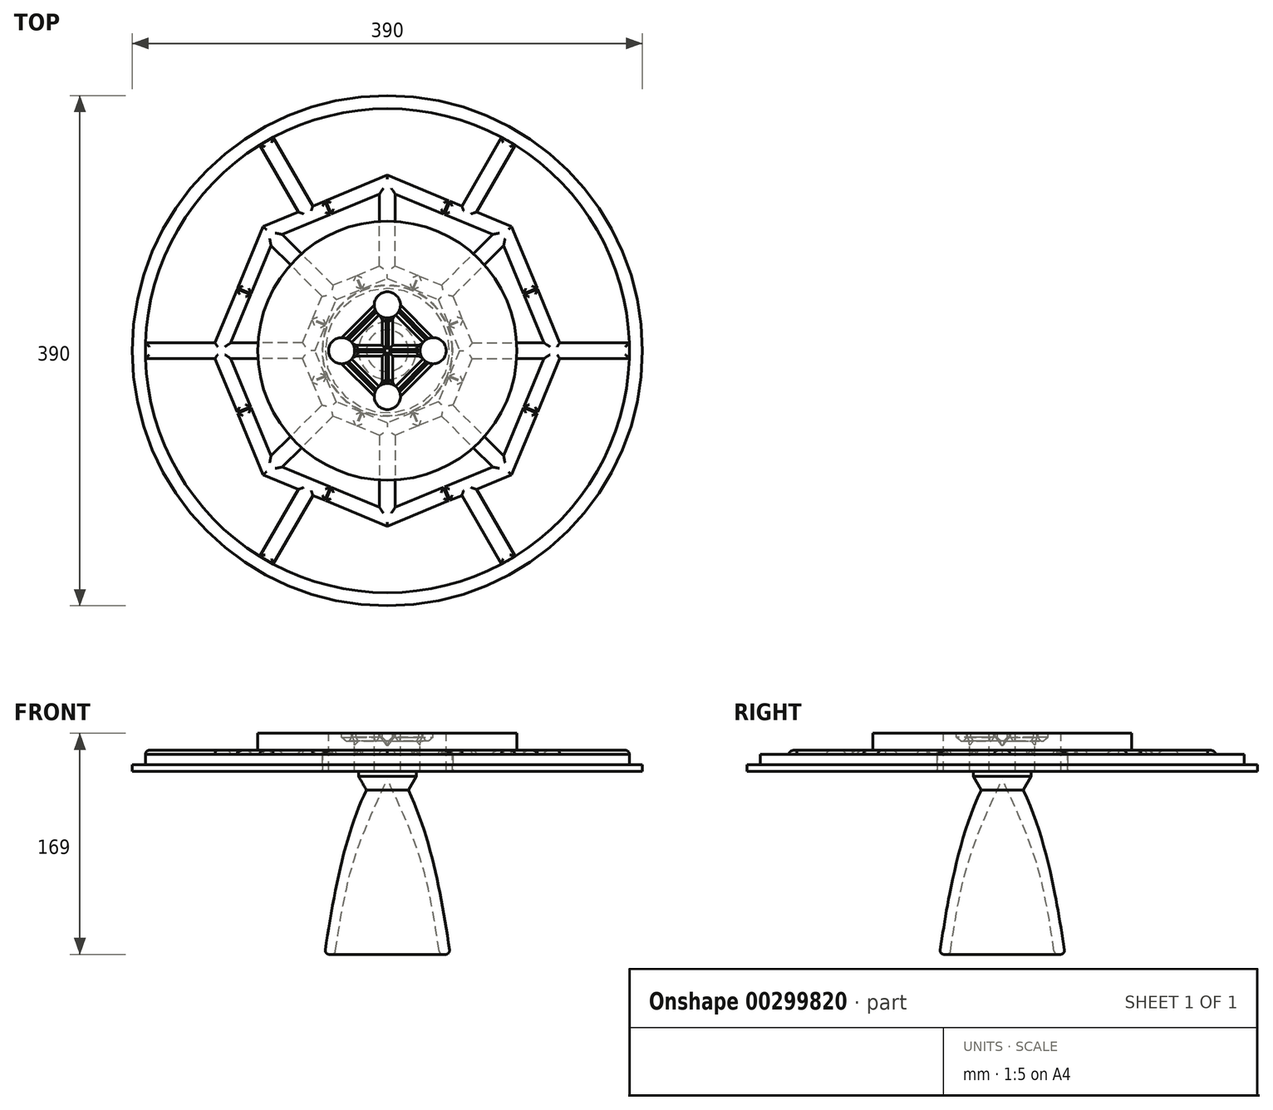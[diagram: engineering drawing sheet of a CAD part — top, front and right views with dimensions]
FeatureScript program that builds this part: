
annotation { "Feature Type Name" : "Feature", "Feature Type Description" : "" }
export const myFeature = defineFeature(function(context is Context, id is Id, definition is map)
    precondition{}
    {
        {
            var Q0;
            Q0=qCreatedBy(makeId("Front.planeOp"),FACE);
            var sketch = newSketch(context, id + "F0", { "sketchPlane" : qUnion([Q0])});
            skLineSegment(sketch, "E0.MirrorCS", {"start": v(50, 0) * mm, "end": v(195, 0) * mm});
            skLineSegment(sketch, "E1", {"start": v(0, 0) * mm, "end": v(0, 0) * mm});
            skLineSegment(sketch, "E2.MirrorCS", {"start": v(195, 0) * mm, "end": v(195, 5) * mm});
            skLineSegment(sketch, "E3.MirrorCS", {"start": v(50, 13) * mm, "end": v(185, 13) * mm});
            skLineSegment(sketch, "E4.MirrorCS", {"start": v(185, 5) * mm, "end": v(195, 5) * mm});
            skLineSegment(sketch, "E5.MirrorCS", {"start": v(185, 13) * mm, "end": v(185, 5) * mm});
            skLineSegment(sketch, "E6.MirrorCS", {"start": v(50, 0) * mm, "end": v(50, 13) * mm});
            skLineSegment(sketch, "E7", {"start": v(0, 0) * mm, "end": v(0, 16.1) * mm});
            skLineSegment(sketch, "E8", {"start": v(0, 0) * mm, "end": v(50, 0) * mm});
            skSolve(sketch);
        }
        {
            var Q0;
            Q0 = qSketchRegion(id + "F0", true);
            var Q1;
            Q1=sQuery(id+"F0.wireOp",EDGE,"E7");
            revolve(context, id + "F1", {"entities" : qUnion([Q0]), "axis" : qUnion([Q1]), "revolveType" : RevolveType.FULL});
        }
        {
            var Q0;
            Q0=makeQuery(id+"F1.opRevolve","SWEPT_FACE",FACE,{"disambiguationData":[OSD([sQuery(id+"F0.wireOp",EDGE,"E3.MirrorCS")])]});
            var sketch = newSketch(context, id + "F2", { "sketchPlane" : qUnion([Q0])});
            skLineSegment(sketch, "E9.0", {"start": v(55.24, 0) * mm, "end": v(47.31, -19.13) * mm});
            skLineSegment(sketch, "E9.7", {"start": v(47.31, 19.13) * mm, "end": v(55.24, 0) * mm});
            skLineSegment(sketch, "E10.0", {"start": v(64.76, -6) * mm, "end": v(57.56, -23.38) * mm});
            skLineSegment(sketch, "E10.7", {"start": v(57.56, 23.38) * mm, "end": v(64.76, 6) * mm});
            skLineSegment(sketch, "E11.0", {"start": v(119.76, -6) * mm, "end": v(104.5, -42.82) * mm});
            skLineSegment(sketch, "E11.7", {"start": v(104.5, 42.82) * mm, "end": v(119.76, 6) * mm});
            skLineSegment(sketch, "E12.0", {"start": v(134.24, 0) * mm, "end": v(114.75, -47.06) * mm});
            skLineSegment(sketch, "E12.7", {"start": v(114.75, 47.06) * mm, "end": v(134.24, 0) * mm});
            skLineSegment(sketch, "E13", {"start": v(64.76, 6) * mm, "end": v(119.76, 6) * mm});
            skLineSegment(sketch, "E14", {"start": v(64.76, -6) * mm, "end": v(119.76, -6) * mm});
            skLineSegment(sketch, "E15", {"start": v(47.31, 19.13) * mm, "end": v(57.56, 23.38) * mm});
            skLineSegment(sketch, "E16", {"start": v(47.31, -19.13) * mm, "end": v(57.56, -23.38) * mm});
            skLineSegment(sketch, "E17.trimOffspring", {"start": v(104.5, 42.82) * mm, "end": v(114.75, 47.06) * mm});
            skLineSegment(sketch, "E18.trimOffspring", {"start": v(104.5, -42.82) * mm, "end": v(114.75, -47.06) * mm});
            skLineSegment(sketch, "E19.1.0", {"start": v(94.92, 94.92) * mm, "end": v(114.42, 47.86) * mm});
            skLineSegment(sketch, "E19.1.1", {"start": v(43.61, 104.17) * mm, "end": v(80.44, 88.92) * mm});
            skLineSegment(sketch, "E19.1.2", {"start": v(46.99, 19.93) * mm, "end": v(57.23, 24.17) * mm});
            skLineSegment(sketch, "E19.1.3", {"start": v(41.55, 50.03) * mm, "end": v(80.44, 88.92) * mm});
            skLineSegment(sketch, "E19.1.4", {"start": v(50.03, 41.55) * mm, "end": v(88.92, 80.44) * mm});
            skLineSegment(sketch, "E19.1.5", {"start": v(50.03, 41.55) * mm, "end": v(57.23, 24.17) * mm});
            skLineSegment(sketch, "E19.1.6", {"start": v(43.61, 104.17) * mm, "end": v(47.86, 114.42) * mm});
            skLineSegment(sketch, "E19.1.7", {"start": v(39.06, 39.06) * mm, "end": v(46.99, 19.93) * mm});
            skLineSegment(sketch, "E19.1.8", {"start": v(47.86, 114.42) * mm, "end": v(94.92, 94.92) * mm});
            skLineSegment(sketch, "E19.1.9", {"start": v(19.93, 46.99) * mm, "end": v(39.06, 39.06) * mm});
            skLineSegment(sketch, "E19.1.10", {"start": v(104.17, 43.61) * mm, "end": v(114.42, 47.86) * mm});
            skLineSegment(sketch, "E19.1.11", {"start": v(24.17, 57.23) * mm, "end": v(41.55, 50.03) * mm});
            skLineSegment(sketch, "E19.1.12", {"start": v(88.92, 80.44) * mm, "end": v(104.17, 43.61) * mm});
            skLineSegment(sketch, "E19.1.13", {"start": v(19.93, 46.99) * mm, "end": v(24.17, 57.23) * mm});
            skLineSegment(sketch, "E19.2.0", {"start": v(0, 134.24) * mm, "end": v(47.06, 114.75) * mm});
            skLineSegment(sketch, "E19.2.1", {"start": v(-42.82, 104.5) * mm, "end": v(-6, 119.76) * mm});
            skLineSegment(sketch, "E19.2.2", {"start": v(19.13, 47.31) * mm, "end": v(23.38, 57.56) * mm});
            skLineSegment(sketch, "E19.2.3", {"start": v(-6, 64.76) * mm, "end": v(-6, 119.76) * mm});
            skLineSegment(sketch, "E19.2.4", {"start": v(6, 64.76) * mm, "end": v(6, 119.76) * mm});
            skLineSegment(sketch, "E19.2.5", {"start": v(6, 64.76) * mm, "end": v(23.38, 57.56) * mm});
            skLineSegment(sketch, "E19.2.6", {"start": v(-42.82, 104.5) * mm, "end": v(-47.06, 114.75) * mm});
            skLineSegment(sketch, "E19.2.7", {"start": v(0, 55.24) * mm, "end": v(19.13, 47.31) * mm});
            skLineSegment(sketch, "E19.2.8", {"start": v(-47.06, 114.75) * mm, "end": v(0, 134.24) * mm});
            skLineSegment(sketch, "E19.2.9", {"start": v(-19.13, 47.31) * mm, "end": v(0, 55.24) * mm});
            skLineSegment(sketch, "E19.2.10", {"start": v(42.82, 104.5) * mm, "end": v(47.06, 114.75) * mm});
            skLineSegment(sketch, "E19.2.11", {"start": v(-23.38, 57.56) * mm, "end": v(-6, 64.76) * mm});
            skLineSegment(sketch, "E19.2.12", {"start": v(6, 119.76) * mm, "end": v(42.82, 104.5) * mm});
            skLineSegment(sketch, "E19.2.13", {"start": v(-19.13, 47.31) * mm, "end": v(-23.38, 57.56) * mm});
            skLineSegment(sketch, "E19.3.0", {"start": v(-94.92, 94.92) * mm, "end": v(-47.86, 114.42) * mm});
            skLineSegment(sketch, "E19.3.1", {"start": v(-104.17, 43.61) * mm, "end": v(-88.92, 80.44) * mm});
            skLineSegment(sketch, "E19.3.2", {"start": v(-19.93, 46.99) * mm, "end": v(-24.17, 57.23) * mm});
            skLineSegment(sketch, "E19.3.3", {"start": v(-50.03, 41.55) * mm, "end": v(-88.92, 80.44) * mm});
            skLineSegment(sketch, "E19.3.4", {"start": v(-41.55, 50.03) * mm, "end": v(-80.44, 88.92) * mm});
            skLineSegment(sketch, "E19.3.5", {"start": v(-41.55, 50.03) * mm, "end": v(-24.17, 57.23) * mm});
            skLineSegment(sketch, "E19.3.6", {"start": v(-104.17, 43.61) * mm, "end": v(-114.42, 47.86) * mm});
            skLineSegment(sketch, "E19.3.7", {"start": v(-39.06, 39.06) * mm, "end": v(-19.93, 46.99) * mm});
            skLineSegment(sketch, "E19.3.8", {"start": v(-114.42, 47.86) * mm, "end": v(-94.92, 94.92) * mm});
            skLineSegment(sketch, "E19.3.9", {"start": v(-46.99, 19.93) * mm, "end": v(-39.06, 39.06) * mm});
            skLineSegment(sketch, "E19.3.10", {"start": v(-43.61, 104.17) * mm, "end": v(-47.86, 114.42) * mm});
            skLineSegment(sketch, "E19.3.11", {"start": v(-57.23, 24.17) * mm, "end": v(-50.03, 41.55) * mm});
            skLineSegment(sketch, "E19.3.12", {"start": v(-80.44, 88.92) * mm, "end": v(-43.61, 104.17) * mm});
            skLineSegment(sketch, "E19.3.13", {"start": v(-46.99, 19.93) * mm, "end": v(-57.23, 24.17) * mm});
            skLineSegment(sketch, "E19.4.0", {"start": v(-134.24, 0) * mm, "end": v(-114.75, 47.06) * mm});
            skLineSegment(sketch, "E19.4.1", {"start": v(-104.5, -42.82) * mm, "end": v(-119.76, -6) * mm});
            skLineSegment(sketch, "E19.4.2", {"start": v(-47.31, 19.13) * mm, "end": v(-57.56, 23.38) * mm});
            skLineSegment(sketch, "E19.4.3", {"start": v(-64.76, -6) * mm, "end": v(-119.76, -6) * mm});
            skLineSegment(sketch, "E19.4.4", {"start": v(-64.76, 6) * mm, "end": v(-119.76, 6) * mm});
            skLineSegment(sketch, "E19.4.5", {"start": v(-64.76, 6) * mm, "end": v(-57.56, 23.38) * mm});
            skLineSegment(sketch, "E19.4.6", {"start": v(-104.5, -42.82) * mm, "end": v(-114.75, -47.06) * mm});
            skLineSegment(sketch, "E19.4.7", {"start": v(-55.24, 0) * mm, "end": v(-47.31, 19.13) * mm});
            skLineSegment(sketch, "E19.4.8", {"start": v(-114.75, -47.06) * mm, "end": v(-134.24, 0) * mm});
            skLineSegment(sketch, "E19.4.9", {"start": v(-47.31, -19.13) * mm, "end": v(-55.24, 0) * mm});
            skLineSegment(sketch, "E19.4.10", {"start": v(-104.5, 42.82) * mm, "end": v(-114.75, 47.06) * mm});
            skLineSegment(sketch, "E19.4.11", {"start": v(-57.56, -23.38) * mm, "end": v(-64.76, -6) * mm});
            skLineSegment(sketch, "E19.4.12", {"start": v(-119.76, 6) * mm, "end": v(-104.5, 42.82) * mm});
            skLineSegment(sketch, "E19.4.13", {"start": v(-47.31, -19.13) * mm, "end": v(-57.56, -23.38) * mm});
            skLineSegment(sketch, "E19.5.0", {"start": v(-94.92, -94.92) * mm, "end": v(-114.42, -47.86) * mm});
            skLineSegment(sketch, "E19.5.1", {"start": v(-43.61, -104.17) * mm, "end": v(-80.44, -88.92) * mm});
            skLineSegment(sketch, "E19.5.2", {"start": v(-46.99, -19.93) * mm, "end": v(-57.23, -24.17) * mm});
            skLineSegment(sketch, "E19.5.3", {"start": v(-41.55, -50.03) * mm, "end": v(-80.44, -88.92) * mm});
            skLineSegment(sketch, "E19.5.4", {"start": v(-50.03, -41.55) * mm, "end": v(-88.92, -80.44) * mm});
            skLineSegment(sketch, "E19.5.5", {"start": v(-50.03, -41.55) * mm, "end": v(-57.23, -24.17) * mm});
            skLineSegment(sketch, "E19.5.6", {"start": v(-43.61, -104.17) * mm, "end": v(-47.86, -114.42) * mm});
            skLineSegment(sketch, "E19.5.7", {"start": v(-39.06, -39.06) * mm, "end": v(-46.99, -19.93) * mm});
            skLineSegment(sketch, "E19.5.8", {"start": v(-47.86, -114.42) * mm, "end": v(-94.92, -94.92) * mm});
            skLineSegment(sketch, "E19.5.9", {"start": v(-19.93, -46.99) * mm, "end": v(-39.06, -39.06) * mm});
            skLineSegment(sketch, "E19.5.10", {"start": v(-104.17, -43.61) * mm, "end": v(-114.42, -47.86) * mm});
            skLineSegment(sketch, "E19.5.11", {"start": v(-24.17, -57.23) * mm, "end": v(-41.55, -50.03) * mm});
            skLineSegment(sketch, "E19.5.12", {"start": v(-88.92, -80.44) * mm, "end": v(-104.17, -43.61) * mm});
            skLineSegment(sketch, "E19.5.13", {"start": v(-19.93, -46.99) * mm, "end": v(-24.17, -57.23) * mm});
            skLineSegment(sketch, "E19.6.0", {"start": v(0, -134.24) * mm, "end": v(-47.06, -114.75) * mm});
            skLineSegment(sketch, "E19.6.1", {"start": v(42.82, -104.5) * mm, "end": v(6, -119.76) * mm});
            skLineSegment(sketch, "E19.6.2", {"start": v(-19.13, -47.31) * mm, "end": v(-23.38, -57.56) * mm});
            skLineSegment(sketch, "E19.6.3", {"start": v(6, -64.76) * mm, "end": v(6, -119.76) * mm});
            skLineSegment(sketch, "E19.6.4", {"start": v(-6, -64.76) * mm, "end": v(-6, -119.76) * mm});
            skLineSegment(sketch, "E19.6.5", {"start": v(-6, -64.76) * mm, "end": v(-23.38, -57.56) * mm});
            skLineSegment(sketch, "E19.6.6", {"start": v(42.82, -104.5) * mm, "end": v(47.06, -114.75) * mm});
            skLineSegment(sketch, "E19.6.7", {"start": v(0, -55.24) * mm, "end": v(-19.13, -47.31) * mm});
            skLineSegment(sketch, "E19.6.8", {"start": v(47.06, -114.75) * mm, "end": v(0, -134.24) * mm});
            skLineSegment(sketch, "E19.6.9", {"start": v(19.13, -47.31) * mm, "end": v(0, -55.24) * mm});
            skLineSegment(sketch, "E19.6.10", {"start": v(-42.82, -104.5) * mm, "end": v(-47.06, -114.75) * mm});
            skLineSegment(sketch, "E19.6.11", {"start": v(23.38, -57.56) * mm, "end": v(6, -64.76) * mm});
            skLineSegment(sketch, "E19.6.12", {"start": v(-6, -119.76) * mm, "end": v(-42.82, -104.5) * mm});
            skLineSegment(sketch, "E19.6.13", {"start": v(19.13, -47.31) * mm, "end": v(23.38, -57.56) * mm});
            skLineSegment(sketch, "E19.7.0", {"start": v(94.92, -94.92) * mm, "end": v(47.86, -114.42) * mm});
            skLineSegment(sketch, "E19.7.1", {"start": v(104.17, -43.61) * mm, "end": v(88.92, -80.44) * mm});
            skLineSegment(sketch, "E19.7.2", {"start": v(19.93, -46.99) * mm, "end": v(24.17, -57.23) * mm});
            skLineSegment(sketch, "E19.7.3", {"start": v(50.03, -41.55) * mm, "end": v(88.92, -80.44) * mm});
            skLineSegment(sketch, "E19.7.4", {"start": v(41.55, -50.03) * mm, "end": v(80.44, -88.92) * mm});
            skLineSegment(sketch, "E19.7.5", {"start": v(41.55, -50.03) * mm, "end": v(24.17, -57.23) * mm});
            skLineSegment(sketch, "E19.7.6", {"start": v(104.17, -43.61) * mm, "end": v(114.42, -47.86) * mm});
            skLineSegment(sketch, "E19.7.7", {"start": v(39.06, -39.06) * mm, "end": v(19.93, -46.99) * mm});
            skLineSegment(sketch, "E19.7.8", {"start": v(114.42, -47.86) * mm, "end": v(94.92, -94.92) * mm});
            skLineSegment(sketch, "E19.7.9", {"start": v(46.99, -19.93) * mm, "end": v(39.06, -39.06) * mm});
            skLineSegment(sketch, "E19.7.10", {"start": v(43.61, -104.17) * mm, "end": v(47.86, -114.42) * mm});
            skLineSegment(sketch, "E19.7.11", {"start": v(57.23, -24.17) * mm, "end": v(50.03, -41.55) * mm});
            skLineSegment(sketch, "E19.7.12", {"start": v(80.44, -88.92) * mm, "end": v(43.61, -104.17) * mm});
            skLineSegment(sketch, "E19.7.13", {"start": v(46.99, -19.93) * mm, "end": v(57.23, -24.17) * mm});
            skPoint(sketch, "E19.center", {"position": v(0, 0) * mm});
            skSolve(sketch);
        }
        {
            var Q0;
            Q0 = qSketchRegion(id + "F2", true);
            extrude(context, id + "F3", {"entities" : qUnion([Q0]), "operationType" : NewBodyOperationType.ADD, "depth" : 3 * mm});
        }
        {
            var Q0;
            Q0=makeQuery(id+"F1.opRevolve","SWEPT_FACE",FACE,{"disambiguationData":[OSD([sQuery(id+"F0.wireOp",EDGE,"E3.MirrorCS")])]});
            var sketch = newSketch(context, id + "F4", { "sketchPlane" : qUnion([Q0])});
            skLineSegment(sketch, "E20", {"start": v(119.9, 0) * mm, "end": v(119.9, -6) * mm});
            skLineSegment(sketch, "E21", {"start": v(119.9, -6) * mm, "end": v(184.9, -6) * mm});
            skLineSegment(sketch, "E22.MirrorCS", {"start": v(119.9, 6) * mm, "end": v(184.9, 6) * mm});
            skLineSegment(sketch, "E23.MirrorCS", {"start": v(119.9, 0) * mm, "end": v(119.9, 6) * mm});
            skLineSegment(sketch, "E24", {"start": v(184.9, 6) * mm, "end": v(184.9, -6) * mm});
            skLineSegment(sketch, "E25.1.0", {"start": v(87.26, 163.13) * mm, "end": v(97.65, 157.13) * mm});
            skLineSegment(sketch, "E25.1.1", {"start": v(65.15, 100.84) * mm, "end": v(97.65, 157.13) * mm});
            skLineSegment(sketch, "E25.1.2", {"start": v(59.95, 103.84) * mm, "end": v(54.76, 106.84) * mm});
            skLineSegment(sketch, "E25.1.3", {"start": v(59.95, 103.84) * mm, "end": v(65.15, 100.84) * mm});
            skLineSegment(sketch, "E25.1.4", {"start": v(54.76, 106.84) * mm, "end": v(87.26, 163.13) * mm});
            skLineSegment(sketch, "E25.2.0", {"start": v(-97.65, 157.13) * mm, "end": v(-87.26, 163.13) * mm});
            skLineSegment(sketch, "E25.2.1", {"start": v(-54.76, 106.84) * mm, "end": v(-87.26, 163.13) * mm});
            skLineSegment(sketch, "E25.2.2", {"start": v(-59.95, 103.84) * mm, "end": v(-65.15, 100.84) * mm});
            skLineSegment(sketch, "E25.2.3", {"start": v(-59.95, 103.84) * mm, "end": v(-54.76, 106.84) * mm});
            skLineSegment(sketch, "E25.2.4", {"start": v(-65.15, 100.84) * mm, "end": v(-97.65, 157.13) * mm});
            skLineSegment(sketch, "E25.3.0", {"start": v(-184.9, -6) * mm, "end": v(-184.9, 6) * mm});
            skLineSegment(sketch, "E25.3.1", {"start": v(-119.9, 6) * mm, "end": v(-184.9, 6) * mm});
            skLineSegment(sketch, "E25.3.2", {"start": v(-119.9, 0) * mm, "end": v(-119.9, -6) * mm});
            skLineSegment(sketch, "E25.3.3", {"start": v(-119.9, 0) * mm, "end": v(-119.9, 6) * mm});
            skLineSegment(sketch, "E25.3.4", {"start": v(-119.9, -6) * mm, "end": v(-184.9, -6) * mm});
            skLineSegment(sketch, "E25.4.0", {"start": v(-87.26, -163.13) * mm, "end": v(-97.65, -157.13) * mm});
            skLineSegment(sketch, "E25.4.1", {"start": v(-65.15, -100.84) * mm, "end": v(-97.65, -157.13) * mm});
            skLineSegment(sketch, "E25.4.2", {"start": v(-59.95, -103.84) * mm, "end": v(-54.76, -106.84) * mm});
            skLineSegment(sketch, "E25.4.3", {"start": v(-59.95, -103.84) * mm, "end": v(-65.15, -100.84) * mm});
            skLineSegment(sketch, "E25.4.4", {"start": v(-54.76, -106.84) * mm, "end": v(-87.26, -163.13) * mm});
            skLineSegment(sketch, "E25.5.0", {"start": v(97.65, -157.13) * mm, "end": v(87.26, -163.13) * mm});
            skLineSegment(sketch, "E25.5.1", {"start": v(54.76, -106.84) * mm, "end": v(87.26, -163.13) * mm});
            skLineSegment(sketch, "E25.5.2", {"start": v(59.95, -103.84) * mm, "end": v(65.15, -100.84) * mm});
            skLineSegment(sketch, "E25.5.3", {"start": v(59.95, -103.84) * mm, "end": v(54.76, -106.84) * mm});
            skLineSegment(sketch, "E25.5.4", {"start": v(65.15, -100.84) * mm, "end": v(97.65, -157.13) * mm});
            skPoint(sketch, "E25.center", {"position": v(0, 0) * mm});
            skSolve(sketch);
        }
        {
            var Q0;
            Q0 = qSketchRegion(id + "F4", true);
            extrude(context, id + "F5", {"entities" : qUnion([Q0]), "operationType" : NewBodyOperationType.ADD, "depth" : 3 * mm});
        }
        {
            var Q0;
            Q0=makeQuery(id+"F5.boolean.opBoolean","MERGE",FACE,{"derivedFrom":[makeQuery(id+"F3.opExtrude","CAP_FACE",FACE,{"disambiguationData":[OSD([sQuery(id+"F2.wireOp",EDGE,"E19.4.0"),sQuery(id+"F2.wireOp",EDGE,"E19.4.1"),sQuery(id+"F2.wireOp",EDGE,"E19.4.2"),sQuery(id+"F2.wireOp",EDGE,"E19.4.3"),sQuery(id+"F2.wireOp",EDGE,"E19.4.4"),sQuery(id+"F2.wireOp",EDGE,"E19.4.5"),sQuery(id+"F2.wireOp",EDGE,"E19.4.6"),sQuery(id+"F2.wireOp",EDGE,"E19.4.7"),sQuery(id+"F2.wireOp",EDGE,"E19.4.8"),sQuery(id+"F2.wireOp",EDGE,"E19.4.9"),sQuery(id+"F2.wireOp",EDGE,"E19.4.10"),sQuery(id+"F2.wireOp",EDGE,"E19.4.11"),sQuery(id+"F2.wireOp",EDGE,"E19.4.12"),sQuery(id+"F2.wireOp",EDGE,"E19.4.13")])],"isStart":false}),makeQuery(id+"F5.opExtrude","CAP_FACE",FACE,{"disambiguationData":[OSD([sQuery(id+"F4.wireOp",EDGE,"E25.3.0"),sQuery(id+"F4.wireOp",EDGE,"E25.3.1"),sQuery(id+"F4.wireOp",EDGE,"E25.3.2"),sQuery(id+"F4.wireOp",EDGE,"E25.3.3"),sQuery(id+"F4.wireOp",EDGE,"E25.3.4")])],"isStart":false})]});
            var Q1;
            Q1=makeQuery(id+"F5.boolean.opBoolean","MERGE",FACE,{"derivedFrom":[makeQuery(id+"F3.opExtrude","CAP_FACE",FACE,{"disambiguationData":[OSD([sQuery(id+"F2.wireOp",EDGE,"E19.3.0"),sQuery(id+"F2.wireOp",EDGE,"E19.3.1"),sQuery(id+"F2.wireOp",EDGE,"E19.3.2"),sQuery(id+"F2.wireOp",EDGE,"E19.3.3"),sQuery(id+"F2.wireOp",EDGE,"E19.3.4"),sQuery(id+"F2.wireOp",EDGE,"E19.3.5"),sQuery(id+"F2.wireOp",EDGE,"E19.3.6"),sQuery(id+"F2.wireOp",EDGE,"E19.3.7"),sQuery(id+"F2.wireOp",EDGE,"E19.3.8"),sQuery(id+"F2.wireOp",EDGE,"E19.3.9"),sQuery(id+"F2.wireOp",EDGE,"E19.3.10"),sQuery(id+"F2.wireOp",EDGE,"E19.3.11"),sQuery(id+"F2.wireOp",EDGE,"E19.3.12"),sQuery(id+"F2.wireOp",EDGE,"E19.3.13")])],"isStart":false}),makeQuery(id+"F5.opExtrude","CAP_FACE",FACE,{"disambiguationData":[OSD([sQuery(id+"F4.wireOp",EDGE,"E25.2.0"),sQuery(id+"F4.wireOp",EDGE,"E25.2.1"),sQuery(id+"F4.wireOp",EDGE,"E25.2.2"),sQuery(id+"F4.wireOp",EDGE,"E25.2.3"),sQuery(id+"F4.wireOp",EDGE,"E25.2.4")])],"isStart":false})]});
            var Q2;
            Q2=makeQuery(id+"F3.opExtrude","CAP_FACE",FACE,{"disambiguationData":[OSD([sQuery(id+"F2.wireOp",EDGE,"E19.2.0"),sQuery(id+"F2.wireOp",EDGE,"E19.2.1"),sQuery(id+"F2.wireOp",EDGE,"E19.2.2"),sQuery(id+"F2.wireOp",EDGE,"E19.2.3"),sQuery(id+"F2.wireOp",EDGE,"E19.2.4"),sQuery(id+"F2.wireOp",EDGE,"E19.2.5"),sQuery(id+"F2.wireOp",EDGE,"E19.2.6"),sQuery(id+"F2.wireOp",EDGE,"E19.2.7"),sQuery(id+"F2.wireOp",EDGE,"E19.2.8"),sQuery(id+"F2.wireOp",EDGE,"E19.2.9"),sQuery(id+"F2.wireOp",EDGE,"E19.2.10"),sQuery(id+"F2.wireOp",EDGE,"E19.2.11"),sQuery(id+"F2.wireOp",EDGE,"E19.2.12"),sQuery(id+"F2.wireOp",EDGE,"E19.2.13")])],"isStart":false});
            var Q3;
            Q3=makeQuery(id+"F5.boolean.opBoolean","MERGE",FACE,{"derivedFrom":[makeQuery(id+"F3.opExtrude","CAP_FACE",FACE,{"disambiguationData":[OSD([sQuery(id+"F2.wireOp",EDGE,"E19.1.0"),sQuery(id+"F2.wireOp",EDGE,"E19.1.1"),sQuery(id+"F2.wireOp",EDGE,"E19.1.2"),sQuery(id+"F2.wireOp",EDGE,"E19.1.3"),sQuery(id+"F2.wireOp",EDGE,"E19.1.4"),sQuery(id+"F2.wireOp",EDGE,"E19.1.5"),sQuery(id+"F2.wireOp",EDGE,"E19.1.6"),sQuery(id+"F2.wireOp",EDGE,"E19.1.7"),sQuery(id+"F2.wireOp",EDGE,"E19.1.8"),sQuery(id+"F2.wireOp",EDGE,"E19.1.9"),sQuery(id+"F2.wireOp",EDGE,"E19.1.10"),sQuery(id+"F2.wireOp",EDGE,"E19.1.11"),sQuery(id+"F2.wireOp",EDGE,"E19.1.12"),sQuery(id+"F2.wireOp",EDGE,"E19.1.13")])],"isStart":false}),makeQuery(id+"F5.opExtrude","CAP_FACE",FACE,{"disambiguationData":[OSD([sQuery(id+"F4.wireOp",EDGE,"E25.1.0"),sQuery(id+"F4.wireOp",EDGE,"E25.1.1"),sQuery(id+"F4.wireOp",EDGE,"E25.1.2"),sQuery(id+"F4.wireOp",EDGE,"E25.1.3"),sQuery(id+"F4.wireOp",EDGE,"E25.1.4")])],"isStart":false})]});
            var Q4;
            Q4=makeQuery(id+"F5.boolean.opBoolean","MERGE",FACE,{"derivedFrom":[makeQuery(id+"F3.opExtrude","CAP_FACE",FACE,{"disambiguationData":[OSD([sQuery(id+"F2.wireOp",EDGE,"E9.0"),sQuery(id+"F2.wireOp",EDGE,"E9.7"),sQuery(id+"F2.wireOp",EDGE,"E10.0"),sQuery(id+"F2.wireOp",EDGE,"E10.7"),sQuery(id+"F2.wireOp",EDGE,"E11.0"),sQuery(id+"F2.wireOp",EDGE,"E11.7"),sQuery(id+"F2.wireOp",EDGE,"E12.0"),sQuery(id+"F2.wireOp",EDGE,"E12.7"),sQuery(id+"F2.wireOp",EDGE,"E13"),sQuery(id+"F2.wireOp",EDGE,"E14"),sQuery(id+"F2.wireOp",EDGE,"E15"),sQuery(id+"F2.wireOp",EDGE,"E16"),sQuery(id+"F2.wireOp",EDGE,"E17.trimOffspring"),sQuery(id+"F2.wireOp",EDGE,"E18.trimOffspring")])],"isStart":false}),makeQuery(id+"F5.opExtrude","CAP_FACE",FACE,{"disambiguationData":[OSD([sQuery(id+"F4.wireOp",EDGE,"E20"),sQuery(id+"F4.wireOp",EDGE,"E21"),sQuery(id+"F4.wireOp",EDGE,"E22.MirrorCS"),sQuery(id+"F4.wireOp",EDGE,"E23.MirrorCS"),sQuery(id+"F4.wireOp",EDGE,"E24")])],"isStart":false})]});
            var Q5;
            Q5=makeQuery(id+"F5.boolean.opBoolean","MERGE",FACE,{"derivedFrom":[makeQuery(id+"F3.opExtrude","CAP_FACE",FACE,{"disambiguationData":[OSD([sQuery(id+"F2.wireOp",EDGE,"E19.7.0"),sQuery(id+"F2.wireOp",EDGE,"E19.7.1"),sQuery(id+"F2.wireOp",EDGE,"E19.7.2"),sQuery(id+"F2.wireOp",EDGE,"E19.7.3"),sQuery(id+"F2.wireOp",EDGE,"E19.7.4"),sQuery(id+"F2.wireOp",EDGE,"E19.7.5"),sQuery(id+"F2.wireOp",EDGE,"E19.7.6"),sQuery(id+"F2.wireOp",EDGE,"E19.7.7"),sQuery(id+"F2.wireOp",EDGE,"E19.7.8"),sQuery(id+"F2.wireOp",EDGE,"E19.7.9"),sQuery(id+"F2.wireOp",EDGE,"E19.7.10"),sQuery(id+"F2.wireOp",EDGE,"E19.7.11"),sQuery(id+"F2.wireOp",EDGE,"E19.7.12"),sQuery(id+"F2.wireOp",EDGE,"E19.7.13")])],"isStart":false}),makeQuery(id+"F5.opExtrude","CAP_FACE",FACE,{"disambiguationData":[OSD([sQuery(id+"F4.wireOp",EDGE,"E25.5.0"),sQuery(id+"F4.wireOp",EDGE,"E25.5.1"),sQuery(id+"F4.wireOp",EDGE,"E25.5.2"),sQuery(id+"F4.wireOp",EDGE,"E25.5.3"),sQuery(id+"F4.wireOp",EDGE,"E25.5.4")])],"isStart":false})]});
            var Q6;
            Q6=makeQuery(id+"F3.opExtrude","CAP_FACE",FACE,{"disambiguationData":[OSD([sQuery(id+"F2.wireOp",EDGE,"E19.6.0"),sQuery(id+"F2.wireOp",EDGE,"E19.6.1"),sQuery(id+"F2.wireOp",EDGE,"E19.6.2"),sQuery(id+"F2.wireOp",EDGE,"E19.6.3"),sQuery(id+"F2.wireOp",EDGE,"E19.6.4"),sQuery(id+"F2.wireOp",EDGE,"E19.6.5"),sQuery(id+"F2.wireOp",EDGE,"E19.6.6"),sQuery(id+"F2.wireOp",EDGE,"E19.6.7"),sQuery(id+"F2.wireOp",EDGE,"E19.6.8"),sQuery(id+"F2.wireOp",EDGE,"E19.6.9"),sQuery(id+"F2.wireOp",EDGE,"E19.6.10"),sQuery(id+"F2.wireOp",EDGE,"E19.6.11"),sQuery(id+"F2.wireOp",EDGE,"E19.6.12"),sQuery(id+"F2.wireOp",EDGE,"E19.6.13")])],"isStart":false});
            var Q7;
            Q7=makeQuery(id+"F5.boolean.opBoolean","MERGE",FACE,{"derivedFrom":[makeQuery(id+"F3.opExtrude","CAP_FACE",FACE,{"disambiguationData":[OSD([sQuery(id+"F2.wireOp",EDGE,"E19.5.0"),sQuery(id+"F2.wireOp",EDGE,"E19.5.1"),sQuery(id+"F2.wireOp",EDGE,"E19.5.2"),sQuery(id+"F2.wireOp",EDGE,"E19.5.3"),sQuery(id+"F2.wireOp",EDGE,"E19.5.4"),sQuery(id+"F2.wireOp",EDGE,"E19.5.5"),sQuery(id+"F2.wireOp",EDGE,"E19.5.6"),sQuery(id+"F2.wireOp",EDGE,"E19.5.7"),sQuery(id+"F2.wireOp",EDGE,"E19.5.8"),sQuery(id+"F2.wireOp",EDGE,"E19.5.9"),sQuery(id+"F2.wireOp",EDGE,"E19.5.10"),sQuery(id+"F2.wireOp",EDGE,"E19.5.11"),sQuery(id+"F2.wireOp",EDGE,"E19.5.12"),sQuery(id+"F2.wireOp",EDGE,"E19.5.13")])],"isStart":false}),makeQuery(id+"F5.opExtrude","CAP_FACE",FACE,{"disambiguationData":[OSD([sQuery(id+"F4.wireOp",EDGE,"E25.4.0"),sQuery(id+"F4.wireOp",EDGE,"E25.4.1"),sQuery(id+"F4.wireOp",EDGE,"E25.4.2"),sQuery(id+"F4.wireOp",EDGE,"E25.4.3"),sQuery(id+"F4.wireOp",EDGE,"E25.4.4")])],"isStart":false})]});
            fillet(context, id + "F6", {"entities" : qUnion([Q0, Q1, Q2, Q3, Q4, Q5, Q6, Q7]), "radius" : 3 * mm, "tangentPropagation" : true, "allowEdgeOverflow" : false});
        }
        {
            var Q0;
            Q0=qCreatedBy(makeId("Front.planeOp"),FACE);
            var sketch = newSketch(context, id + "F7", { "sketchPlane" : qUnion([Q0])});
            skLineSegment(sketch, "E26", {"start": v(0, 0) * mm, "end": v(0, 29) * mm});
            skLineSegment(sketch, "E27", {"start": v(0, 29) * mm, "end": v(99, 29) * mm});
            skLineSegment(sketch, "E28", {"start": v(99, 29) * mm, "end": v(99, 16) * mm});
            skLineSegment(sketch, "E29", {"start": v(99, 16) * mm, "end": v(49.6, 16) * mm});
            skLineSegment(sketch, "E30", {"start": v(49.6, 16) * mm, "end": v(49.6, 0) * mm});
            skLineSegment(sketch, "E31", {"start": v(22, 0) * mm, "end": v(22, -4) * mm});
            skLineSegment(sketch, "E32", {"start": v(22, -4) * mm, "end": v(16, -14.4) * mm});
            skLineSegment(sketch, "E33", {"start": v(0, 0) * mm, "end": v(0, -6) * mm});
            skFitSpline(sketch, "E34", {"points": [v(16, -14.4) * mm, v(35.04, -70) * mm, v(48, -140) * mm], "startDerivative": vector(47.96, -98.6) * mm, "endDerivative": vector(18.7, -125.17) * mm});
            skFitSpline(sketch, "E35", {"points": [v(40, -140) * mm, v(26.13, -70) * mm, v(0, -6) * mm], "startDerivative": vector(-21.37, 141.56) * mm, "endDerivative": vector(-58.69, 128.47) * mm});
            skLineSegment(sketch, "E36", {"start": v(40, -140) * mm, "end": v(48, -140) * mm});
            skLineSegment(sketch, "E37", {"start": v(22, 0) * mm, "end": v(49.6, 0) * mm});
            skSolve(sketch);
        }
        {
            var Q0;
            Q0 = qSketchRegion(id + "F7", true);
            var Q1;
            Q1=sQuery(id+"F7.wireOp",EDGE,"E26");
            revolve(context, id + "F8", {"entities" : qUnion([Q0]), "axis" : qUnion([Q1]), "revolveType" : RevolveType.FULL});
        }
        {
            var Q0;
            Q0=makeQuery(id+"F8.opRevolve","SWEPT_FACE",FACE,{"disambiguationData":[OSD([sQuery(id+"F7.wireOp",EDGE,"E36")])]});
            fillet(context, id + "F9", {"entities" : qUnion([Q0]), "radius" : 3 * mm, "tangentPropagation" : true, "allowEdgeOverflow" : false});
        }
        {
            var Q0;
            Q0=makeQuery(id+"F8.opRevolve","SWEPT_FACE",FACE,{"disambiguationData":[OSD([sQuery(id+"F7.wireOp",EDGE,"E27")])]});
            var sketch = newSketch(context, id + "F10", { "sketchPlane" : qUnion([Q0])});
            skCircle(sketch, "E38", {"center": v(35, 0) * mm, "radius": 10 * mm});
            skCircle(sketch, "E39.1.0", {"center": v(0, 35) * mm, "radius": 10 * mm});
            skCircle(sketch, "E39.2.0", {"center": v(-35, 0) * mm, "radius": 10 * mm});
            skCircle(sketch, "E39.3.0", {"center": v(0, -35) * mm, "radius": 10 * mm});
            skPoint(sketch, "E39.center", {"position": v(0, 0) * mm});
            skSolve(sketch);
        }
        {
            var Q0;
            Q0 = qSketchRegion(id + "F10", true);
            extrude(context, id + "F11", {"entities" : qUnion([Q0]), "operationType" : NewBodyOperationType.REMOVE, "oppositeDirection" : true, "depth" : 29 * mm});
        }
        {
            var Q0;
            Q0=makeQuery(id+"F8.opRevolve","SWEPT_FACE",FACE,{"disambiguationData":[OSD([sQuery(id+"F7.wireOp",EDGE,"E27")])]});
            var sketch = newSketch(context, id + "F12", { "sketchPlane" : qUnion([Q0])});
            skLineSegment(sketch, "E40", {"start": v(0, 45) * mm, "end": v(45, 0) * mm});
            skLineSegment(sketch, "E41", {"start": v(45, 0) * mm, "end": v(0, -45) * mm});
            skLineSegment(sketch, "E42", {"start": v(0, -45) * mm, "end": v(-45, 0) * mm});
            skLineSegment(sketch, "E43", {"start": v(-45, 0) * mm, "end": v(0, 45) * mm});
            skLineSegment(sketch, "E44", {"start": v(4, 29.69) * mm, "end": v(33.69, 0) * mm});
            skLineSegment(sketch, "E45", {"start": v(29.69, -4) * mm, "end": v(0, -33.69) * mm});
            skLineSegment(sketch, "E46", {"start": v(-4, -29.69) * mm, "end": v(-33.69, 0) * mm});
            skLineSegment(sketch, "E47", {"start": v(-29.69, 4) * mm, "end": v(0, 33.69) * mm});
            skLineSegment(sketch, "E48", {"start": v(-29.69, 4) * mm, "end": v(-4, 4) * mm});
            skLineSegment(sketch, "E49", {"start": v(-29.69, -4) * mm, "end": v(-4, -4) * mm});
            skLineSegment(sketch, "E50", {"start": v(-4, 29.69) * mm, "end": v(-4, 4) * mm});
            skLineSegment(sketch, "E51", {"start": v(4, 29.69) * mm, "end": v(4, 4) * mm});
            skLineSegment(sketch, "E52.trimOffspring", {"start": v(4, 4) * mm, "end": v(29.69, 4) * mm});
            skLineSegment(sketch, "E53.trimOffspring", {"start": v(-4, -4) * mm, "end": v(-4, -29.69) * mm});
            skLineSegment(sketch, "E54.trimOffspring", {"start": v(4, -4) * mm, "end": v(4, -29.69) * mm});
            skLineSegment(sketch, "E55.trimOffspring", {"start": v(4, -4) * mm, "end": v(29.69, -4) * mm});
            skSolve(sketch);
        }
        {
            var Q0;
            Q0 = qSketchRegion(id + "F12", true);
            extrude(context, id + "F13", {"entities" : qUnion([Q0]), "operationType" : NewBodyOperationType.REMOVE, "oppositeDirection" : true, "depth" : 6 * mm, "offsetDistance" : 25 * mm});
        }
        {
            var Q0;
            Q0=makeQuery(id+"F13.boolean.opBoolean","COPY",EDGE,{"derivedFrom":makeQuery(id+"F13.opExtrude","CAP_EDGE",EDGE,{"disambiguationData":[OSD([sQuery(id+"F12.wireOp",EDGE,"E40")])],"isStart":false})});
            var Q1;
            Q1=makeQuery(id+"F13.boolean.opBoolean","COPY",EDGE,{"derivedFrom":makeQuery(id+"F13.opExtrude","CAP_EDGE",EDGE,{"disambiguationData":[OSD([sQuery(id+"F12.wireOp",EDGE,"E44")])],"isStart":false})});
            var Q2;
            Q2=makeQuery(id+"F13.boolean.opBoolean","COPY",EDGE,{"derivedFrom":makeQuery(id+"F13.opExtrude","CAP_EDGE",EDGE,{"disambiguationData":[OSD([sQuery(id+"F12.wireOp",EDGE,"E45")])],"isStart":false})});
            var Q3;
            Q3=makeQuery(id+"F13.boolean.opBoolean","COPY",EDGE,{"derivedFrom":makeQuery(id+"F13.opExtrude","CAP_EDGE",EDGE,{"disambiguationData":[OSD([sQuery(id+"F12.wireOp",EDGE,"E41")])],"isStart":false})});
            var Q4;
            Q4=makeQuery(id+"F13.boolean.opBoolean","COPY",EDGE,{"derivedFrom":makeQuery(id+"F13.opExtrude","CAP_EDGE",EDGE,{"disambiguationData":[OSD([sQuery(id+"F12.wireOp",EDGE,"E46")])],"isStart":false})});
            var Q5;
            Q5=makeQuery(id+"F13.boolean.opBoolean","COPY",EDGE,{"derivedFrom":makeQuery(id+"F13.opExtrude","CAP_EDGE",EDGE,{"disambiguationData":[OSD([sQuery(id+"F12.wireOp",EDGE,"E42")])],"isStart":false})});
            var Q6;
            Q6=makeQuery(id+"F13.boolean.opBoolean","COPY",EDGE,{"derivedFrom":makeQuery(id+"F13.opExtrude","CAP_EDGE",EDGE,{"disambiguationData":[OSD([sQuery(id+"F12.wireOp",EDGE,"E43")])],"isStart":false})});
            var Q7;
            Q7=makeQuery(id+"F13.boolean.opBoolean","COPY",EDGE,{"derivedFrom":makeQuery(id+"F13.opExtrude","CAP_EDGE",EDGE,{"disambiguationData":[OSD([sQuery(id+"F12.wireOp",EDGE,"E47")])],"isStart":false})});
            var Q8;
            {var subQ0=sQuery(id+"F12.wireOp",EDGE,"E53.trimOffspring");var subQ1=sQuery(id+"F12.wireOp",EDGE,"E52.trimOffspring");var subQ2=sQuery(id+"F12.wireOp",EDGE,"E48");var subQ3=sQuery(id+"F12.wireOp",EDGE,"E49");var subQ4=sQuery(id+"F12.wireOp",EDGE,"E50");var subQ5=sQuery(id+"F12.wireOp",EDGE,"E51");var subQ6=sQuery(id+"F12.wireOp",EDGE,"E54.trimOffspring");var subQ7=sQuery(id+"F12.wireOp",EDGE,"E55.trimOffspring");Q8=makeQuery(id+"F13.boolean.opBoolean","COPY",FACE,{"disambiguationData":[TD([makeQuery(id+"F13.opExtrude","SWEPT_FACE",FACE,{"disambiguationData":[OSD([subQ2])]})])],"derivedFrom":makeQuery(id+"F13.opExtrude","CAP_FACE",FACE,{"disambiguationData":[OSD([sQuery(id+"F12.wireOp",EDGE,"E40"),sQuery(id+"F12.wireOp",EDGE,"E41"),sQuery(id+"F12.wireOp",EDGE,"E42"),sQuery(id+"F12.wireOp",EDGE,"E43"),sQuery(id+"F12.wireOp",EDGE,"E44"),sQuery(id+"F12.wireOp",EDGE,"E45"),sQuery(id+"F12.wireOp",EDGE,"E46"),sQuery(id+"F12.wireOp",EDGE,"E47"),subQ2,subQ3,subQ4,subQ5,subQ1,subQ0,subQ6,subQ7])],"isStart":false})});}
            chamfer(context, id + "F14", {"entities" : qUnion([Q0, Q1, Q2, Q3, Q4, Q5, Q6, Q7, Q8]), "width" : 3 * mm, "tangentPropagation" : true});
        }
    });
